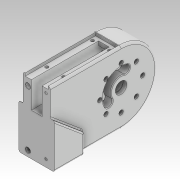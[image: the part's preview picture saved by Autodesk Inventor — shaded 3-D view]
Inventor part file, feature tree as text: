
AUTODESK INVENTOR PART (.ipt)
format: ipt  version: 2020 (Build 240168000, 168)  size: 835,072 bytes
history: native  units: mm
features: sketch x30, extrude x28, fillet x5, plane x2, revolve x2, pattern_circular x1, chamfer x1, projected_geometry x1
ambient origin geometry x8: Origin, YZ Plane, XZ Plane, XY Plane, X Axis, Y Axis, Z Axis, Center Point
bodies: Solid1 (feature_tree)
feature tree (70):
  extrude  "Extrusion1"  Depth=250.0mm
  extrude  "Extrusion3"  Depth=50.0mm TaperAngle=0.0deg
  extrude  "Extrusion6"  TaperAngle=0.0deg  [1 undecoded]
  extrude  "Extrusion7"  Depth=50.0mm
  extrude  "Extrusion8"  Depth=10.0mm TaperAngle=0.0deg
  extrude  "Extrusion9"  TaperAngle=0.0deg  [1 undecoded]
  extrude  "Extrusion10"  TaperAngle=30.0deg  [1 undecoded]
  extrude  "Extrusion11"  Depth=16.15mm
  extrude  "Extrusion12"  Depth=60.0mm
  plane  "Work Plane1"
  extrude  "Extrusion13"  Depth=10.0mm TaperAngle=0.0deg
  revolve  "Revolution1"  [1 undecoded]
  extrude  "Extrusion14"  Depth=86.0mm
  extrude  "Extrusion15"  Depth=4.0mm TaperAngle=0.0deg
  extrude  "Extrusion16"  Depth=70.0mm
  revolve  "Revolution2"  [1 undecoded]
  extrude  "Extrusion17"  Depth=7.3mm
  fillet  "Fillet1"  [1 undecoded]
  plane  "Work Plane2"
  extrude  "Extrusion18"  Depth=34.0mm
  extrude  "Extrusion19"  Depth=3.0mm TaperAngle=0.0deg
  extrude  "Extrusion20"  Depth=15.0mm TaperAngle=0.0deg
  extrude  "Extrusion21"  Depth=15.0mm
  extrude  "Extrusion25"  Depth=80.0mm TaperAngle=360.0deg
  extrude  "Extrusion22"  Depth=5.2mm
  fillet  "Fillet2"  Radius=5.2mm
  fillet  "Fillet3"  Radius=1.0mm
  extrude  "Extrusion23"  TaperAngle=90.0deg  [1 undecoded]
  extrude  "Extrusion24"  Depth=5.5mm
  extrude  "Extrusion26"  Depth=19.198622mm
  extrude  "Extrusion27"  Depth=50.0mm
  extrude  "Extrusion28"  TaperAngle=0.0deg  [1 undecoded]
  extrude  "CHOP"  Depth=14.0mm
  extrude  "Extrusion30"  Depth=12.5mm
  extrude  "Extrusion31"  Depth=1.0mm
  fillet  "Fillet4"  Radius=10.0mm
  pattern_circular  "Circular Pattern1"  [2 undecoded]
  chamfer  "Chamfer1"  Distance=32.0mm
  fillet  "Fillet5"  Radius=110.0mm
  sketch  "Sketch1"  dims[d0=50.0mm d1=250.0mm]
  sketch  "Sketch3"  dims[d2=47.2mm d3=50.0mm d4=0.0mm]
  sketch  "Sketch6"  dims[d10=5.0mm d11=0.0mm d12=0.0mm]
  sketch  "Sketch7"  dims[d19=50.0mm d20=0.0mm d21=8.726646mm]
  projected_geometry  "Projected Loop1"
  sketch  "Sketch8"  dims[d22=75.0mm d25=10.0mm d26=0.0mm]
  sketch  "Sketch9"  dims[d27=50.0mm d30=0.0mm d31=0.0mm]
  sketch  "Sketch10"  dims[d33=30.0deg d34=30.0deg]
  sketch  "Sketch11"  dims[d35=0.0mm d36=0.0mm d37=16.15mm]
  sketch  "Sketch12"  dims[d38=3.3mm d39=60.0mm]
  sketch  "Sketch13"  dims[d40=80.0mm d42=360.0deg d44=10.0mm d45=0.0mm]
  sketch  "Sketch14"  dims[d50=42.0mm d51=42.0mm d52=0.0mm d53=0.0mm]
  sketch  "Sketch15"  dims[d54=38.0mm d55=86.0mm]
  sketch  "Sketch16"  dims[d56=59.0mm d57=4.0mm d58=0.0mm]
  sketch  "Sketch17"  dims[d59=-2.0mm d60=70.0mm]
  sketch  "Sketch18"  dims[d61=40.0mm d62=18.0mm d63=0.0mm]
  sketch  "Sketch19"  dims[d64=1.5mm d65=7.3mm d66=90.0deg]
  sketch  "Sketch20"  dims[d67=22.0mm d68=34.0mm]
  sketch  "Sketch21"  dims[d69=3.5mm d70=3.0mm d71=0.0mm]
  sketch  "Sketch22"  dims[d72=0.0mm d73=15.0mm d74=0.0mm]
  sketch  "Sketch23"  dims[d75=15.0mm d76=130.0mm]
  sketch  "Sketch24"  dims[d77=6.0mm d78=80.0mm d80=360.0deg]
  sketch  "Sketch25"  dims[d82=15.0mm d83=0.0mm d84=5.2mm d85=5.2mm d86=1.0mm]
  sketch  "Sketch26"  dims[d87=1.5mm d88=90.0deg]
  sketch  "Sketch27"  dims[d89=5.5mm d90=20.0mm]
  sketch  "Sketch28"  dims[d91=30.0deg d92=19.198622mm]
  sketch  "Sketch29"  dims[d93=15.0mm d94=0.0mm d95=50.0mm]
  sketch  "Sketch30"  dims[d96=30.0mm d97=0.0mm]
  sketch  "Sketch31"  dims[d98=8.0mm d99=14.0mm]
  sketch  "Sketch32"  dims[d100=6.4mm d101=12.5mm]
  sketch  "Sketch33"  dims[d102=130.0mm d103=80.0mm d104=0.0mm d105=0.0mm d106=2.45mm d107=10.0mm d108=10.0mm d109=32.0mm d110=110.0mm d111=0.0mm d112=3.0mm d113=3.0mm d114=5.0mm d115=1.0mm d116=4.0mm d117=0.0mm d118=4.0mm d119=4.0mm d120=32.25mm d121=0.0mm d122=3.0mm d124=0.5mm d125=0.0mm d126=3.0mm d127=2.0mm d128=8.0mm d129=8.0mm d130=4.0mm d131=4.0mm d132=4.3mm d133=6.0mm d134=0.0mm d135=4.0mm d136=0.0mm d137=60.0mm d138=0.5mm d139=0.0mm d140=3.0mm d141=10.0mm d142=20.0mm d143=15.0mm d144=0.0mm d145=8.0mm d146=23.75mm d147=0.0mm d148=15.0mm d149=23.75mm d150=0.0mm d151=200.998mm d152=0.0mm d153=76.0mm d154=4.0mm d155=1.0mm d156=0.0mm d157=22.5mm d158=2.0mm d159=15.0mm d160=0.8mm d161=0.0mm d162=0.2mm d163=80.0mm d164=360.0deg d166=0.5mm d167=2.0mm d168=45.0deg d169=1.0mm d123=0.872665mm]
note: 10 required parameter values undecoded (feature->parameter linkage not recoverable at this tier; creation-order binding heuristic only, values carry confidence <= 0.55)